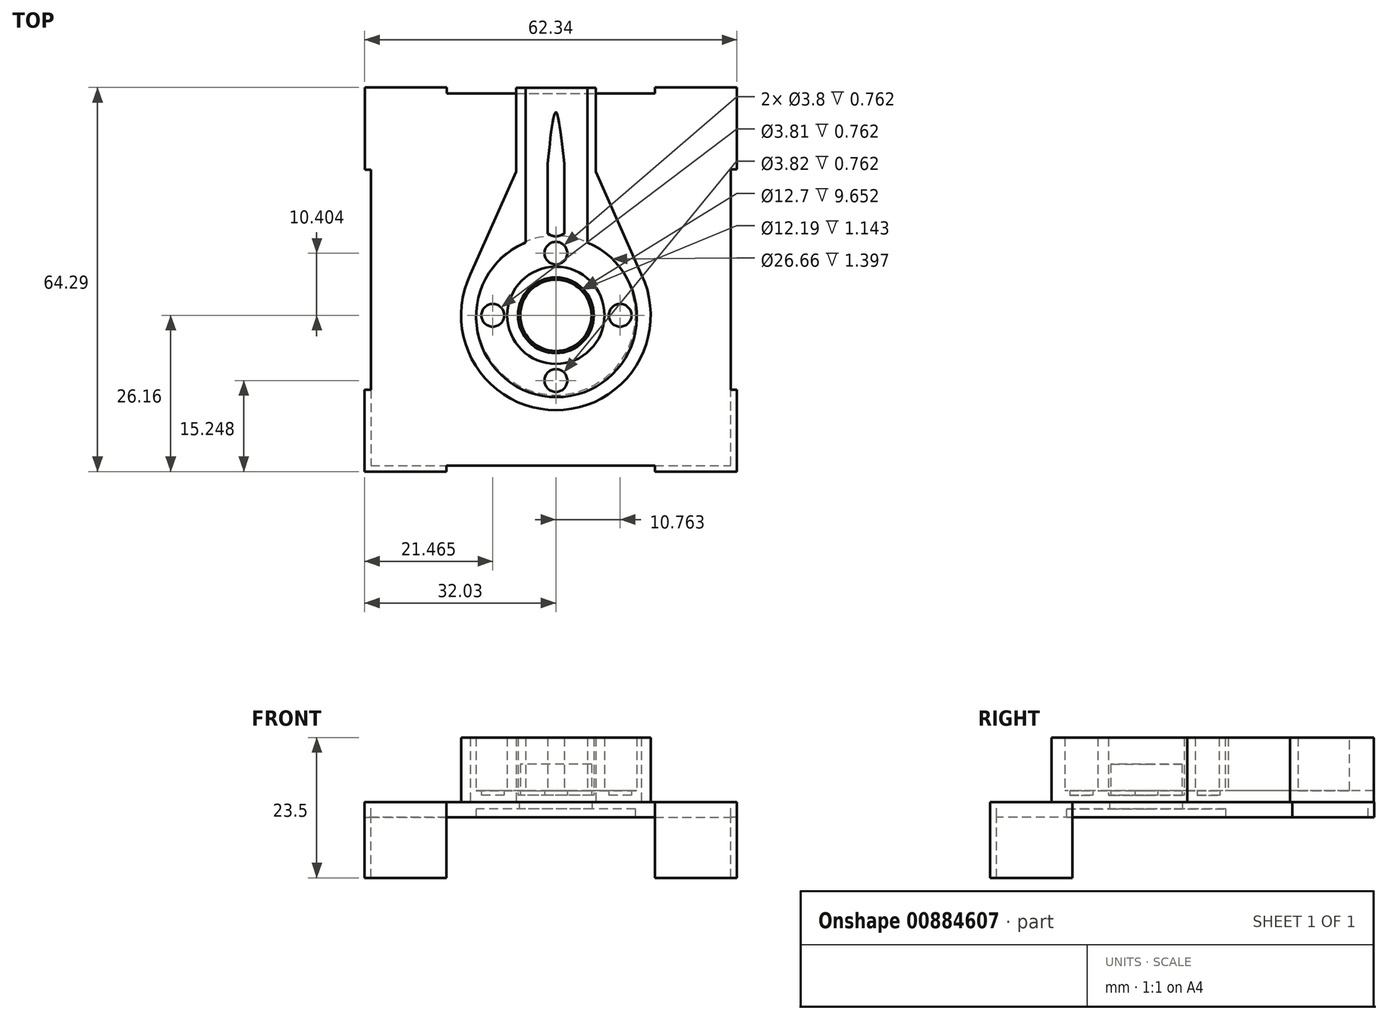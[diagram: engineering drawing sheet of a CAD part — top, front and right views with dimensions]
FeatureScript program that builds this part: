
annotation { "Feature Type Name" : "Feature", "Feature Type Description" : "" }
export const myFeature = defineFeature(function(context is Context, id is Id, definition is map)
    precondition{}
    {
        {
            var Q0;
            Q0=qCreatedBy(makeId("Top.planeOp"),FACE);
            var sketch = newSketch(context, id + "F0", { "sketchPlane" : qUnion([Q0])});
            skCircle(sketch, "E0", {"center": v(0, 0) * mm, "radius": 8.13 * mm, "construction": true});
            skArc(sketch, "E1", {"start": v(-14.33, 6.83) * mm, "mid": v(0, -15.87) * mm, "end": v(14.33, 6.83) * mm});
            skLineSegment(sketch, "E2.left", {"start": v(-1.4, 13.66) * mm, "end": v(-1.4, 17.27) * mm});
            skLineSegment(sketch, "E2.right", {"start": v(1.4, 13.66) * mm, "end": v(1.4, 17.27) * mm});
            skLineSegment(sketch, "E3.left", {"start": v(-5.08, 12.2) * mm, "end": v(-5.08, 38.1) * mm});
            skLineSegment(sketch, "E3.right", {"start": v(5.28, 12.2) * mm, "end": v(5.28, 38.1) * mm});
            skPoint(sketch, "E4.orphan", {"position": v(-5.08, 0) * mm});
            skPoint(sketch, "E2.bottom.start.orphan", {"position": v(-1.4, 0) * mm});
            skPoint(sketch, "E5.bottom.start.orphan", {"position": v(-9.53, 0) * mm});
            skPoint(sketch, "E6.orphan", {"position": v(9.53, 0) * mm});
            skArc(sketch, "E7.trimOffspring", {"start": v(-5.08, 12.2) * mm, "mid": v(0.1, -13.7) * mm, "end": v(5.28, 12.2) * mm});
            skPoint(sketch, "E8.orphan", {"position": v(15.88, 0) * mm});
            skPoint(sketch, "E9.orphan", {"position": v(-15.88, 0) * mm});
            skFitSpline(sketch, "E10", {"points": [v(-1.4, 13.66) * mm, v(0, 13.2) * mm, v(1.4, 13.66) * mm], "startDerivative": vector(2.8, -1.36) * mm, "endDerivative": vector(2.8, 1.36) * mm});
            skCircle(sketch, "E11", {"center": v(0, 0) * mm, "radius": 6.35 * mm});
            skLineSegment(sketch, "E12", {"start": v(6.66, 38.1) * mm, "end": v(6.66, 24.05) * mm});
            skLineSegment(sketch, "E13", {"start": v(-6.66, 24.03) * mm, "end": v(-14.33, 6.83) * mm});
            skLineSegment(sketch, "E14", {"start": v(6.66, 24.05) * mm, "end": v(14.33, 6.83) * mm});
            skLineSegment(sketch, "E15", {"start": v(-6.66, 38.1) * mm, "end": v(6.66, 38.1) * mm});
            skLineSegment(sketch, "E16.trimOffspring", {"start": v(-6.66, 38.1) * mm, "end": v(-6.66, 24.03) * mm});
            skLineSegment(sketch, "E17", {"start": v(-1.4, 13.66) * mm, "end": v(-1.4, 25.4) * mm});
            skLineSegment(sketch, "E18", {"start": v(1.4, 13.66) * mm, "end": v(1.4, 25.4) * mm});
            skFitSpline(sketch, "E19", {"points": [v(-1.4, 25.4) * mm, v(0, 33.99) * mm, v(1.4, 25.4) * mm], "startDerivative": vector(2.8, 25.77) * mm, "endDerivative": vector(2.8, -25.76) * mm});
            skPoint(sketch, "E20.middle", {"position": v(0, -10.91) * mm});
            skPoint(sketch, "E21.middle", {"position": v(-10.56, 0) * mm});
            skCircle(sketch, "E22", {"center": v(0, -10.91) * mm, "radius": 1.9 * mm});
            skCircle(sketch, "E23", {"center": v(-10.56, 0) * mm, "radius": 1.9 * mm});
            skPoint(sketch, "E24.orphan", {"position": v(-13.36, 0) * mm});
            skPoint(sketch, "E25.orphan", {"position": v(0, -13.7) * mm});
            skCircle(sketch, "E26", {"center": v(0, 10.4) * mm, "radius": 1.9 * mm});
            skCircle(sketch, "E27", {"center": v(10.76, 0) * mm, "radius": 1.9 * mm});
            skCircle(sketch, "E28", {"center": v(0, 0) * mm, "radius": 8.14 * mm});
            skSolve(sketch);
        }
        {
            var Q0;
            Q0=makeQuery(id+"F0.imprint","IMPRINT",FACE,{"disambiguationData":[TD([[makeQuery(id+"F0.imprint","IMPRINT",EDGE,{"derivedFrom":sQuery(id+"F0.wireOp",EDGE,"E1")}),1.0]])]});
            var Q1;
            Q1=makeQuery(id+"F0.imprint","IMPRINT",FACE,{"disambiguationData":[TD([[makeQuery(id+"F0.imprint","IMPRINT",EDGE,{"derivedFrom":sQuery(id+"F0.wireOp",EDGE,"E2.left")}),1.0]])]});
            var Q2;
            Q2=makeQuery(id+"F0.imprint","IMPRINT",FACE,{"disambiguationData":[TD([[makeQuery(id+"F0.imprint","IMPRINT",EDGE,{"derivedFrom":sQuery(id+"F0.wireOp",EDGE,"E2.left")}),-1.0]])]});
            var Q3;
            Q3=makeQuery(id+"F0.imprint","IMPRINT",FACE,{"disambiguationData":[TD([[makeQuery(id+"F0.imprint","IMPRINT",EDGE,{"derivedFrom":sQuery(id+"F0.wireOp",EDGE,"E11")}),-1.0]])]});
            extrude(context, id + "F1", {"entities" : qUnion([Q0, Q1, Q2, Q3]), "depth" : 1.9 * mm, "offsetDistance" : 25.4 * mm});
        }
        {
            var Q0;
            Q0=makeQuery(id+"F0.imprint","IMPRINT",FACE,{"disambiguationData":[TD([[makeQuery(id+"F0.imprint","IMPRINT",EDGE,{"derivedFrom":sQuery(id+"F0.wireOp",EDGE,"E11")}),-1.0]])]});
            var Q1;
            Q1=makeQuery(id+"F0.imprint","IMPRINT",FACE,{"disambiguationData":[TD([[makeQuery(id+"F0.imprint","IMPRINT",EDGE,{"derivedFrom":sQuery(id+"F0.wireOp",EDGE,"E1")}),1.0]])]});
            var Q2;
            Q2=makeQuery(id+"F0.imprint","IMPRINT",FACE,{"disambiguationData":[TD([[makeQuery(id+"F0.imprint","IMPRINT",EDGE,{"derivedFrom":sQuery(id+"F0.wireOp",EDGE,"E2.left")}),-1.0]])]});
            extrude(context, id + "F2", {"entities" : qUnion([Q0, Q1, Q2]), "operationType" : NewBodyOperationType.ADD, "depth" : 10.8 * mm, "offsetDistance" : 25.4 * mm});
        }
        {
            var Q0;
            Q0=qCreatedBy(makeId("Top.planeOp"),FACE);
            var sketch = newSketch(context, id + "F3", { "sketchPlane" : qUnion([Q0])});
            skCircle(sketch, "E29", {"center": v(0, 0) * mm, "radius": 13.2 * mm});
            skCircle(sketch, "E30", {"center": v(0, 0) * mm, "radius": 5.97 * mm});
            skSolve(sketch);
        }
        {
            var Q0;
            Q0=qCreatedBy(makeId("Top.planeOp"),FACE);
            var sketch = newSketch(context, id + "F4", { "sketchPlane" : qUnion([Q0])});
            skLineSegment(sketch, "E31.top", {"start": v(-31, -25.14) * mm, "end": v(0, -25.14) * mm});
            skLineSegment(sketch, "E31.left", {"start": v(-31, 0) * mm, "end": v(-31, -25.14) * mm});
            skLineSegment(sketch, "E32.bottom", {"start": v(-18.3, -25.14) * mm, "end": v(29.28, -25.14) * mm});
            skLineSegment(sketch, "E32.top", {"start": v(-31, 37.1) * mm, "end": v(29.28, 37.1) * mm});
            skLineSegment(sketch, "E32.left", {"start": v(-31, -12.43) * mm, "end": v(-31, 37.1) * mm});
            skLineSegment(sketch, "E32.right", {"start": v(29.28, -25.14) * mm, "end": v(29.28, 37.1) * mm});
            skLineSegment(sketch, "E33", {"start": v(-31, -12.43) * mm, "end": v(-32.03, -12.43) * mm});
            skLineSegment(sketch, "E34", {"start": v(-32.03, -12.43) * mm, "end": v(-32.03, -25.14) * mm});
            skLineSegment(sketch, "E35", {"start": v(-18.3, -25.14) * mm, "end": v(-18.3, -26.16) * mm});
            skLineSegment(sketch, "E36", {"start": v(-18.3, -26.16) * mm, "end": v(-31, -26.16) * mm});
            skLineSegment(sketch, "E37", {"start": v(-32.03, -25.14) * mm, "end": v(-32.03, -26.16) * mm});
            skLineSegment(sketch, "E38", {"start": v(-32.03, -26.16) * mm, "end": v(-31, -26.16) * mm});
            skLineSegment(sketch, "E39", {"start": v(16.57, -25.14) * mm, "end": v(16.57, -26.16) * mm});
            skLineSegment(sketch, "E40", {"start": v(16.57, -26.16) * mm, "end": v(29.28, -26.16) * mm});
            skLineSegment(sketch, "E41", {"start": v(30.28, -25.14) * mm, "end": v(30.28, -12.43) * mm});
            skLineSegment(sketch, "E42", {"start": v(30.28, -12.43) * mm, "end": v(29.28, -12.43) * mm});
            skLineSegment(sketch, "E43", {"start": v(29.28, -26.16) * mm, "end": v(30.28, -26.16) * mm});
            skLineSegment(sketch, "E44", {"start": v(30.28, -26.16) * mm, "end": v(30.28, -25.14) * mm});
            skLineSegment(sketch, "E45", {"start": v(-31, 37.1) * mm, "end": v(-18.3, 37.1) * mm});
            skLineSegment(sketch, "E46", {"start": v(-18.3, 37.1) * mm, "end": v(-18.3, 38.13) * mm});
            skLineSegment(sketch, "E47", {"start": v(-18.3, 38.13) * mm, "end": v(-31, 38.13) * mm});
            skLineSegment(sketch, "E48", {"start": v(-32.01, 37.1) * mm, "end": v(-32.01, 38.13) * mm});
            skLineSegment(sketch, "E49", {"start": v(-32.01, 38.13) * mm, "end": v(-31, 38.13) * mm});
            skLineSegment(sketch, "E50", {"start": v(-32.01, 37.1) * mm, "end": v(-32.01, 24.4) * mm});
            skLineSegment(sketch, "E51", {"start": v(-32.01, 24.4) * mm, "end": v(-31, 24.4) * mm});
            skLineSegment(sketch, "E52", {"start": v(29.28, 37.1) * mm, "end": v(16.57, 37.1) * mm});
            skLineSegment(sketch, "E53", {"start": v(16.57, 37.1) * mm, "end": v(16.57, 38.12) * mm});
            skLineSegment(sketch, "E54", {"start": v(16.57, 38.12) * mm, "end": v(29.28, 38.12) * mm});
            skLineSegment(sketch, "E55", {"start": v(30.3, 37.1) * mm, "end": v(30.3, 24.42) * mm});
            skLineSegment(sketch, "E56", {"start": v(30.3, 24.42) * mm, "end": v(29.28, 24.42) * mm});
            skLineSegment(sketch, "E57", {"start": v(29.28, 38.12) * mm, "end": v(30.3, 38.12) * mm});
            skLineSegment(sketch, "E58", {"start": v(30.3, 38.12) * mm, "end": v(30.3, 37.1) * mm});
            skCircle(sketch, "E59", {"center": v(0, 0) * mm, "radius": 13.33 * mm});
            skCircle(sketch, "E60", {"center": v(0, 0) * mm, "radius": 6.1 * mm});
            skSolve(sketch);
        }
        {
            var Q0;
            Q0=makeQuery(id+"F3.imprint","IMPRINT",FACE,{"disambiguationData":[TD([[makeQuery(id+"F3.imprint","IMPRINT",EDGE,{"derivedFrom":sQuery(id+"F3.wireOp",EDGE,"E30")}),1.0]])]});
            extrude(context, id + "F5", {"entities" : qUnion([Q0]), "depth" : 6.35 * mm, "offsetDistance" : 25.4 * mm});
        }
        {
            var Q0;
            Q0 = qSketchRegion(id + "F3", true);
            extrude(context, id + "F6", {"entities" : qUnion([Q0]), "operationType" : NewBodyOperationType.ADD, "depth" : 1.14 * mm, "offsetDistance" : 25.4 * mm});
        }
        {
            var Q0;
            Q0=makeQuery(id+"F4.imprint","IMPRINT",FACE,{"disambiguationData":[TD([[makeQuery(id+"F4.imprint","IMPRINT",EDGE,{"derivedFrom":sQuery(id+"F4.wireOp",EDGE,"E59")}),1.0]])]});
            var Q1;
            {var subQ10=sQuery(id+"F4.wireOp",EDGE,"E31.top");Q1=makeQuery(id+"F4.imprint","IMPRINT",FACE,{"disambiguationData":[TD([[makeQuery(id+"F4.imprint","IMPRINT",EDGE,{"derivedFrom":subQ10}),1.0]])]});}
            var Q2;
            {var subQ0=sQuery(id+"F4.wireOp",EDGE,"E39");Q2=makeQuery(id+"F4.imprint","IMPRINT",FACE,{"disambiguationData":[TD([[makeQuery(id+"F4.imprint","IMPRINT",EDGE,{"derivedFrom":subQ0}),1.0]])]});}
            extrude(context, id + "F7", {"entities" : qUnion([Q0, Q1, Q2]), "oppositeDirection" : true, "depth" : 1.14 * mm, "offsetDistance" : 25.4 * mm});
        }
        {
            var Q0;
            Q0 = qSketchRegion(id + "F4", true);
            extrude(context, id + "F8", {"entities" : qUnion([Q0]), "operationType" : NewBodyOperationType.ADD, "oppositeDirection" : true, "depth" : 2.54 * mm, "offsetDistance" : 25.4 * mm});
        }
        {
            var Q0;
            {var subQ0=sQuery(id+"F4.wireOp",EDGE,"E45");Q0=makeQuery(id+"F4.imprint","IMPRINT",FACE,{"disambiguationData":[TD([[makeQuery(id+"F4.imprint","IMPRINT",EDGE,{"derivedFrom":subQ0}),1.0]])]});}
            var Q1;
            Q1=makeQuery(id+"F4.imprint","IMPRINT",FACE,{"disambiguationData":[TD([[makeQuery(id+"F4.imprint","IMPRINT",EDGE,{"derivedFrom":sQuery(id+"F4.wireOp",EDGE,"E31.top")}),-1.0]])]});
            var Q2;
            {var subQ0=sQuery(id+"F4.wireOp",EDGE,"E39");Q2=makeQuery(id+"F4.imprint","IMPRINT",FACE,{"disambiguationData":[TD([[makeQuery(id+"F4.imprint","IMPRINT",EDGE,{"derivedFrom":subQ0}),1.0]])]});}
            var Q3;
            {var subQ0=sQuery(id+"F4.wireOp",EDGE,"E52");Q3=makeQuery(id+"F4.imprint","IMPRINT",FACE,{"disambiguationData":[TD([[makeQuery(id+"F4.imprint","IMPRINT",EDGE,{"derivedFrom":subQ0}),-1.0]])]});}
            extrude(context, id + "F9", {"entities" : qUnion([Q0, Q1, Q2, Q3]), "operationType" : NewBodyOperationType.ADD, "oppositeDirection" : true, "depth" : 12.7 * mm, "offsetDistance" : 25.4 * mm});
        }
    });
